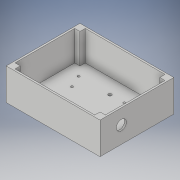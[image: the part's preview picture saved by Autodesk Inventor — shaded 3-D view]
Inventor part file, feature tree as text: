
AUTODESK INVENTOR PART (.ipt)
format: ipt  version: 2018 (Build 220112000, 112)  size: 163,840 bytes
history: native  units: in
note: dims shown in document units (in); Inventor stores cm internally (conversion verified against a paired STEP export)
features: sketch x6, extrude x5
ambient origin geometry x8: Origin, YZ Plane, XZ Plane, XY Plane, X Axis, Y Axis, Z Axis, Center Point
bodies: Solid1 (feature_tree)
feature tree (11):
  extrude  "Extrusion1"  Depth=3.701in
  extrude  "Extrusion2"  Depth=4.527in
  extrude  "Extrusion3"  Depth=0.354in
  extrude  "Extrusion4"  Depth=0.354in
  sketch  "Sketch5"  dims[d11=0.354in d14=1.5in d15=0.0in]
  extrude  "Extrusion5"  Depth=1.5in TaperAngle=0.0deg
  sketch  "Sketch1"  dims[d0=4.705in d1=3.701in]
  sketch  "Sketch2"  dims[d2=0.089in d3=0.0in d4=4.527in]
  sketch  "Sketch3"  dims[d5=3.523in d6=0.354in]
  sketch  "Sketch4"  dims[d7=0.354in d10=0.354in]
  sketch  "Sketch6"  dims[d18=0.164in d19=0.164in d20=0.0in d21=0.0in d22=3.42in d23=2.271in d25=0.787in d30=0.112in d31=0.112in d36=0.112in d37=0.112in d38=0.118in d39=0.118in d40=0.118in d41=0.118in d42=0.0in d43=0.0in d44=0.5in d45=1.5in d46=0.0in]
